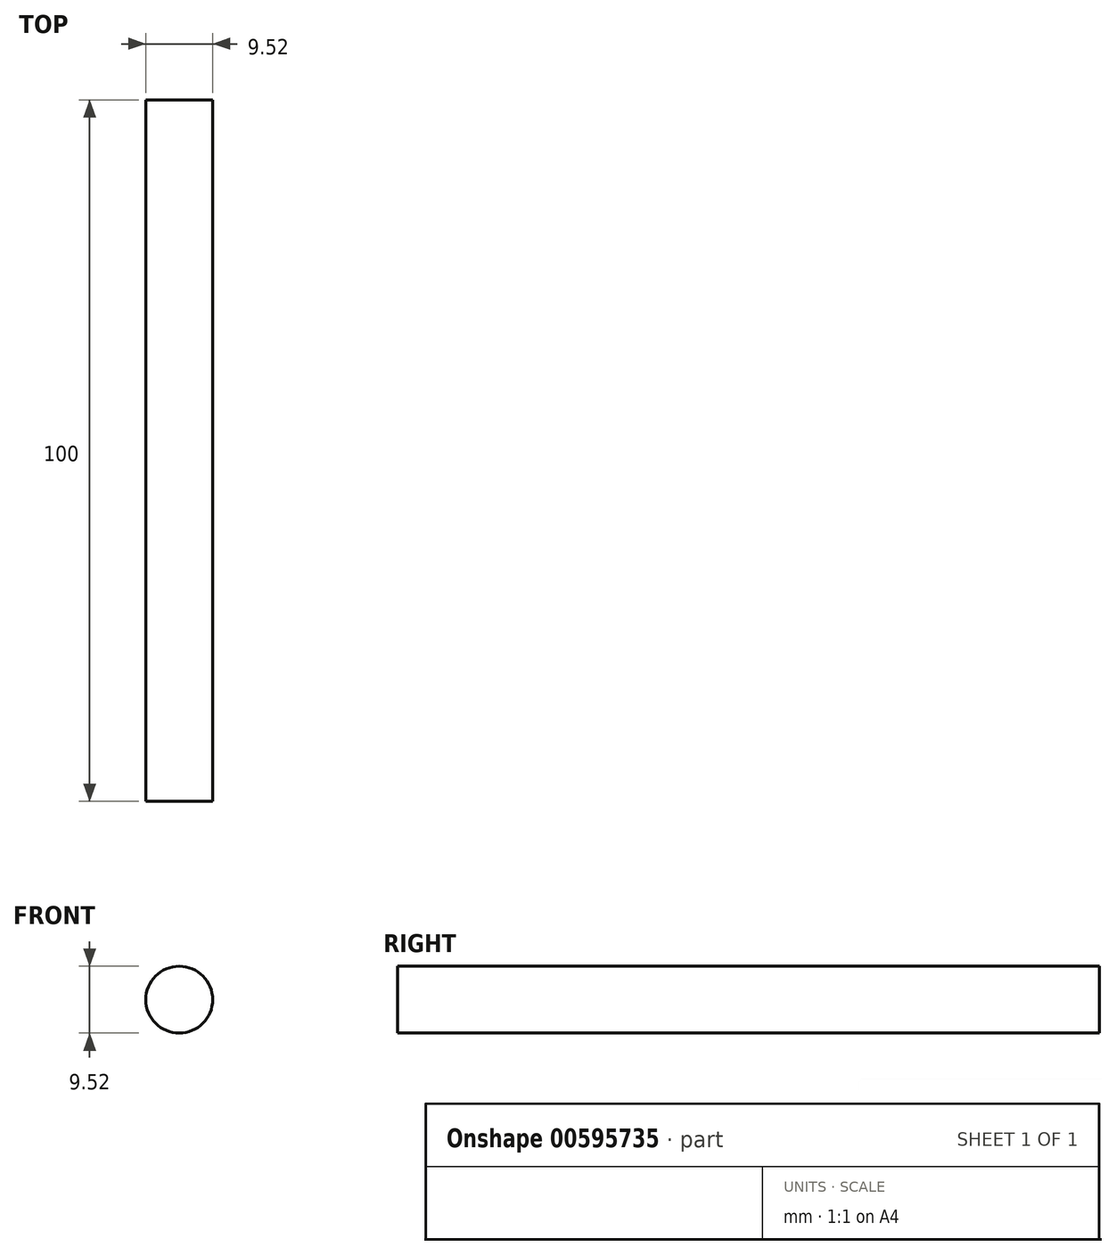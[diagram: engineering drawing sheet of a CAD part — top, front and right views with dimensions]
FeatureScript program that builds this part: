
annotation { "Feature Type Name" : "Feature", "Feature Type Description" : "" }
export const myFeature = defineFeature(function(context is Context, id is Id, definition is map)
    precondition{}
    {
        {
            var Q0;
            Q0=qCreatedBy(makeId("Front.planeOp"),FACE);
            var sketch = newSketch(context, id + "F0", { "sketchPlane" : qUnion([Q0])});
            skCircle(sketch, "E0", {"center": v(0, 0) * mm, "radius": 4.76 * mm});
            skSolve(sketch);
        }
        {
            var Q0;
            Q0=makeQuery(id+"F0.imprint","IMPRINT",FACE,{"disambiguationData":[TD([[makeQuery(id+"F0.imprint","IMPRINT",EDGE,{"derivedFrom":sQuery(id+"F0.wireOp",EDGE,"E0")}),1.0]])]});
            extrude(context, id + "F1", {"entities" : qUnion([Q0]), "depth" : 100 * mm, "offsetDistance" : 25 * mm});
        }
    });
